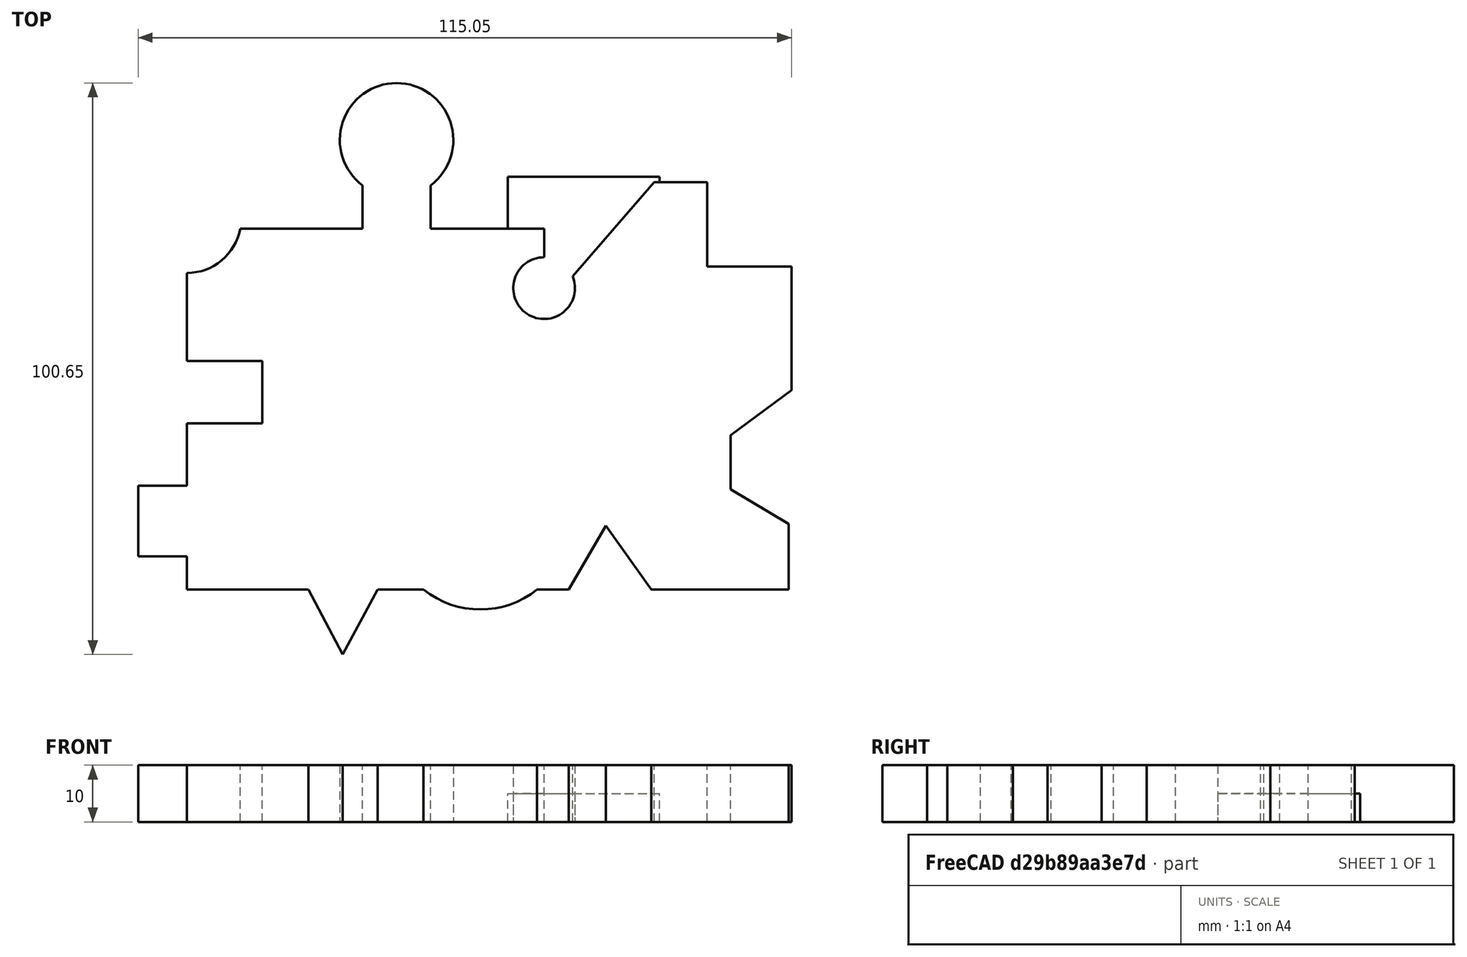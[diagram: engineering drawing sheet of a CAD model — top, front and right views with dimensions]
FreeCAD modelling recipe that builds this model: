
FCSTD DOCUMENT  (FreeCAD 0.17R13327 (Git))
Label: boundarytest
License: All rights reserved
LicenseURL: http://en.wikipedia.org/wiki/All_rights_reserved
objects: Sketcher::SketchObject×1, PartDesign::Pad×1, PartDesign::Body×1, Part::Feature×1
note: 5 computed .brp shape members not serialized (recipe doc carries the construction recipe); baked Part::Feature solids carry a one-line shape summary decoded from their .brp

FEATURE [Sketcher::SketchObject] Sketch
  MapMode = 5
  Support = -> [XY_Plane]
  sketch-geometry (35):
    g0: LineSegment StartX=-51.6702 StartY=0 StartZ=0 EndX=-51.6702 EndY=5.85611 EndZ=0
    g1: LineSegment StartX=-51.6702 StartY=29.2851 StartZ=0 EndX=-38.3996 EndY=29.2851 EndZ=0
    g2: LineSegment StartX=-38.3996 StartY=29.2851 StartZ=0 EndX=-38.3996 EndY=40.2372 EndZ=0
    g3: LineSegment StartX=-38.3996 StartY=40.2372 StartZ=0 EndX=-51.6702 EndY=40.2372 EndZ=0
    g4: LineSegment StartX=-51.6702 StartY=40.2372 StartZ=0 EndX=-51.6702 EndY=55.7701 EndZ=0
    g5: ArcOfCircle CenterX=-51.6702 CenterY=65.2959 CenterZ=0 NormalX=0 NormalY=0 NormalZ=1 AngleXU=0 Radius=9.52575 StartAngle=4.71239 EndAngle=6.1035
    g6: LineSegment StartX=11.2262 StartY=63.5934 StartZ=0 EndX=11.2262 EndY=58.5324 EndZ=0
    g7: ArcOfCircle CenterX=11.2262 CenterY=53.0963 CenterZ=0 NormalX=0 NormalY=0 NormalZ=1 AngleXU=0 Radius=5.43607 StartAngle=1.5708 EndAngle=6.68192
    g8: LineSegment StartX=16.2359 StartY=55.2069 StartZ=0 EndX=30.5922 EndY=71.7337 EndZ=0
    g9: LineSegment StartX=30.5922 StartY=71.7337 StartZ=0 EndX=39.9722 EndY=71.7337 EndZ=0
    g10: LineSegment StartX=39.9722 StartY=71.7337 StartZ=0 EndX=39.9722 EndY=56.9026 EndZ=0
    g11: LineSegment StartX=39.9722 StartY=56.9026 StartZ=0 EndX=54.8033 EndY=56.9026 EndZ=0
    g12: LineSegment StartX=54.8033 StartY=56.9026 StartZ=0 EndX=54.8033 EndY=35.144 EndZ=0
    g13: LineSegment StartX=54.8033 StartY=35.144 StartZ=0 EndX=44.0985 EndY=27.1858 EndZ=0
    g14: LineSegment StartX=44.0985 StartY=27.1858 StartZ=0 EndX=44.0985 EndY=17.636 EndZ=0
    g15: LineSegment StartX=44.0985 StartY=17.636 StartZ=0 EndX=54.285 EndY=11.5878 EndZ=0
    g16: LineSegment StartX=54.285 StartY=11.5878 StartZ=0 EndX=54.285 EndY=0 EndZ=0
    g17: LineSegment StartX=54.285 StartY=0 StartZ=0 EndX=30.0921 EndY=0 EndZ=0
    g18: LineSegment StartX=30.0921 StartY=0 StartZ=0 EndX=22.134 EndY=11.2695 EndZ=0
    g19: LineSegment StartX=22.134 StartY=11.2695 StartZ=0 EndX=15.5437 EndY=0 EndZ=0
    g20: LineSegment StartX=-51.6702 StartY=0 StartZ=0 EndX=-30.2666 EndY=0 EndZ=0
    g21: LineSegment StartX=-42.2978 StartY=63.5934 StartZ=0 EndX=-20.755 EndY=63.5934 EndZ=0
    g22: LineSegment StartX=-8.75501 StartY=63.5934 StartZ=0 EndX=11.2262 EndY=63.5934 EndZ=0
    g23: LineSegment StartX=-20.755 StartY=63.5934 StartZ=0 EndX=-20.755 EndY=71.2179 EndZ=0
    g24: ArcOfCircle CenterX=-14.755 CenterY=79.2179 CenterZ=0 NormalX=0 NormalY=0 NormalZ=1 AngleXU=0 Radius=10 StartAngle=5.35589 EndAngle=10.3521
    g25: LineSegment StartX=-8.75501 StartY=71.2179 StartZ=0 EndX=-8.75501 EndY=63.5934 EndZ=0
    g26: LineSegment StartX=-30.2666 StartY=0 StartZ=0 EndX=-24.2206 EndY=-11.4348 EndZ=0
    g27: LineSegment StartX=-24.2206 StartY=-11.4348 StartZ=0 EndX=-18.0945 EndY=0 EndZ=0
    g28: LineSegment StartX=-18.0945 StartY=0 StartZ=0 EndX=-10 EndY=0 EndZ=0
    g29: LineSegment StartX=-51.6702 StartY=18.3059 StartZ=0 EndX=-60.2493 EndY=18.3059 EndZ=0
    g30: LineSegment StartX=-60.2493 StartY=18.3059 StartZ=0 EndX=-60.2493 EndY=5.85611 EndZ=0
    g31: LineSegment StartX=-60.2493 StartY=5.85611 StartZ=0 EndX=-51.6702 EndY=5.85611 EndZ=0
    g32: LineSegment StartX=-51.6702 StartY=18.3059 StartZ=0 EndX=-51.6702 EndY=29.2851 EndZ=0
    g33: ArcOfCircle CenterX=0 CenterY=12.4793 CenterZ=0 NormalX=0 NormalY=0 NormalZ=1 AngleXU=0 Radius=15.9917 StartAngle=4.03684 EndAngle=5.38794
    g34: LineSegment StartX=10 StartY=0 StartZ=0 EndX=15.5437 EndY=0 EndZ=0
  constraints (69):
    c: PointOnObject(g0,g-1)
    c: Vertical(g0)
    c: Coincident(g32,g1)
    c: Coincident(g1,g2)
    c: Coincident(g2,g3)
    c: Horizontal(g3)
    c: Coincident(g3,g4)
    c: Perpendicular(g4,g5) = 4.71239
    c: Perpendicular(g6,g7) = 4.71239
    c: Coincident(g7,g8)
    c: Coincident(g8,g9)
    c: Horizontal(g9)
    c: Coincident(g9,g10)
    c: Vertical(g10)
    c: Coincident(g10,g11)
    c: Horizontal(g11)
    c: Coincident(g11,g12)
    c: Vertical(g12)
    c: Coincident(g12,g13)
    c: Coincident(g13,g14)
    c: Coincident(g14,g15)
    c: Coincident(g15,g16)
    c: PointOnObject(g16,g-1)
    c: Vertical(g16)
    c: Coincident(g16,g17)
    c: PointOnObject(g17,g-1)
    c: Coincident(g17,g18)
    c: Coincident(g18,g19)
    c: PointOnObject(g19,g-1)
    c: Horizontal(g1)
    c: Vertical(g2)
    c: Vertical(g4)
    c: Vertical(g14)
    c: Equal(g3,g1)
    c: Coincident(g20,g0)
    c: Coincident(g34,g19)
    c: Equal(g10,g11)
    c: Vertical(g6)
    c: Coincident(g5,g21)
    c: Coincident(g22,g6)
    c: Horizontal(g22)
    c: Horizontal(g21)
    c: Tangent(g21,g22) = -1.5708
    c: Coincident(g21,g23)
    c: Vertical(g23)
    c: DistanceX(g21,g22) = 12
    c: Coincident(g23,g24)
    c: Coincident(g24,g25)
    c: Vertical(g25)
    c: Coincident(g22,g25)
    c: Radius(g24) = 10
    c: Equal(g23,g25)
    c: Coincident(g26,g27)
    c: Coincident(g20,g26)
    c: Coincident(g28,g27)
    c: Tangent(g20,g28)
    c: Horizontal(g29)
    c: Coincident(g29,g30)
    c: Vertical(g30)
    c: Coincident(g30,g31)
    c: Horizontal(g31)
    c: Coincident(g0,g31)
    c: Coincident(g32,g29)
    c: Tangent(g0,g32)
    c: PointOnObject(g33,g-2)
    c: Coincident(g28,g33)
    c: Coincident(g34,g33)
    c: Tangent(g28,g34)
    c: DistanceX(g33) = 10
FEATURE [PartDesign::Pad] Pad
  Length = 10
  Length2 = 100
  Profile = -> Sketch
  Type = 0
FEATURE [PartDesign::Body] Body
  Group = -> [Sketch,Pad]
  Origin = -> Origin
  Tip = -> Pad
FEATURE [Part::Feature] Shape
  shape: bbox 26.97 x 25.27 x 5.2 mm, 10 faces (baked)
